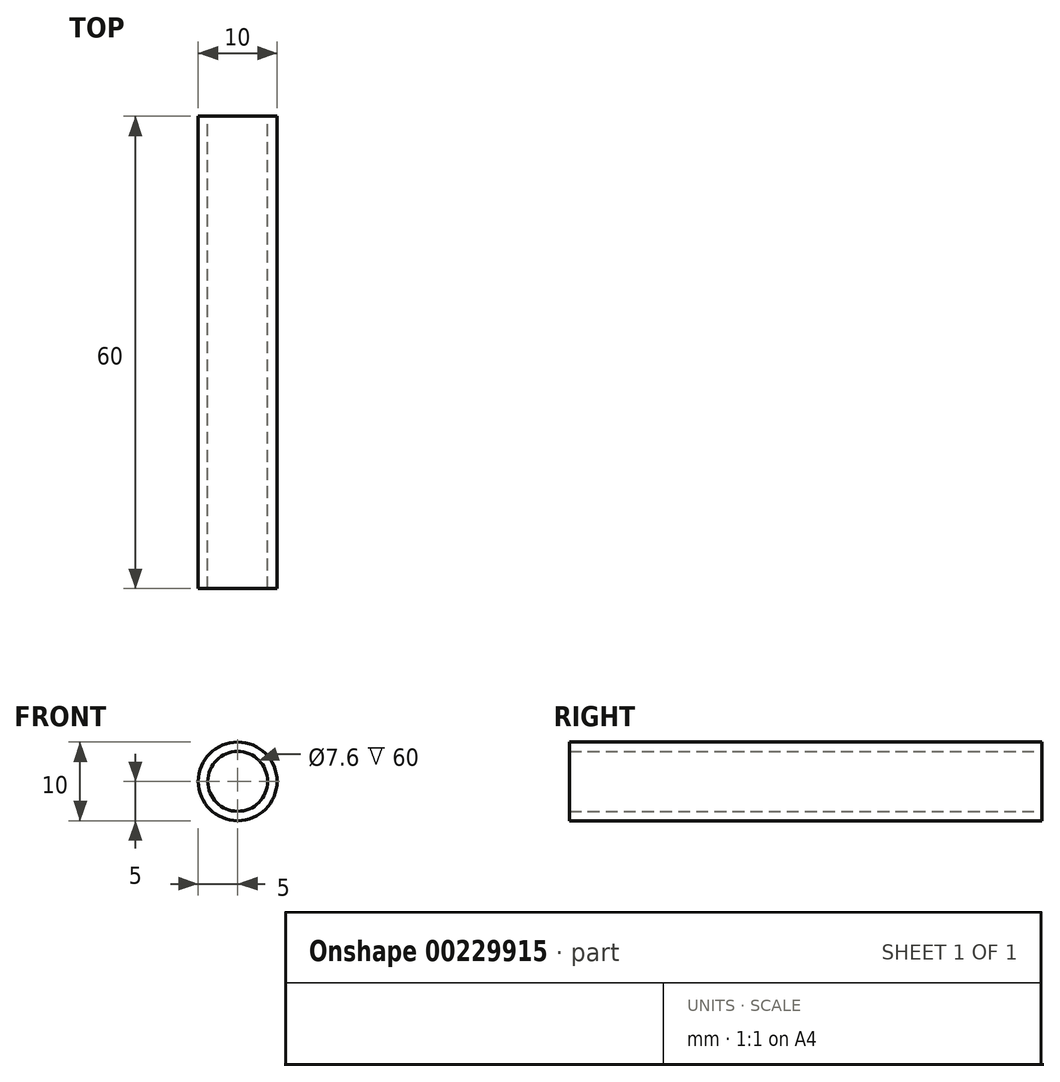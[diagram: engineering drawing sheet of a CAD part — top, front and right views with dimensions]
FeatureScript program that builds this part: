
annotation { "Feature Type Name" : "Feature", "Feature Type Description" : "" }
export const myFeature = defineFeature(function(context is Context, id is Id, definition is map)
    precondition{}
    {
        {
            var Q0;
            Q0=qCreatedBy(makeId("Front.planeOp"),FACE);
            var sketch = newSketch(context, id + "F0", { "sketchPlane" : qUnion([Q0])});
            skCircle(sketch, "E0", {"center": v(0, 0) * mm, "radius": 5 * mm});
            skCircle(sketch, "E1", {"center": v(0, 0) * mm, "radius": 3.8 * mm});
            skSolve(sketch);
        }
        {
            var Q0;
            Q0=qSketchRegion(id+"F0",true);
            extrude(context, id + "F1", {"entities" : qUnion([Q0]), "depth" : 60 * mm});
        }
    });
